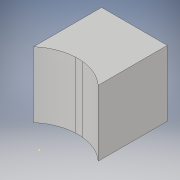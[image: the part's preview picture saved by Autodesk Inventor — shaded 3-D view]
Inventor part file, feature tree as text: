
AUTODESK INVENTOR PART (.ipt)
format: ipt  version: 2019 (Build 230136000, 136)  size: 115,200 bytes
history: native  units: mm
features: sketch x5, hole x3, other x1, extrude x1
ambient origin geometry x8: Origin, YZ Plane, XZ Plane, XY Plane, X Axis, Y Axis, Z Axis, Center Point
bodies: Body1 (feature_tree)
feature tree (10):
  other  "ソリッド1"
  extrude  "押し出し1"  Depth=20.0mm
  sketch  "スケッチ2"
  hole  "穴1"  [1 undecoded]
  hole  "穴2"  [1 undecoded]
  hole  "穴3"  [1 undecoded]
  sketch  "スケッチ1"
  sketch  "スケッチ3"
  sketch  "スケッチ4"
  sketch  "スケッチ5"
note: 3 required parameter values undecoded (feature->parameter linkage not recoverable at this tier; creation-order binding heuristic only, values carry confidence <= 0.55)
